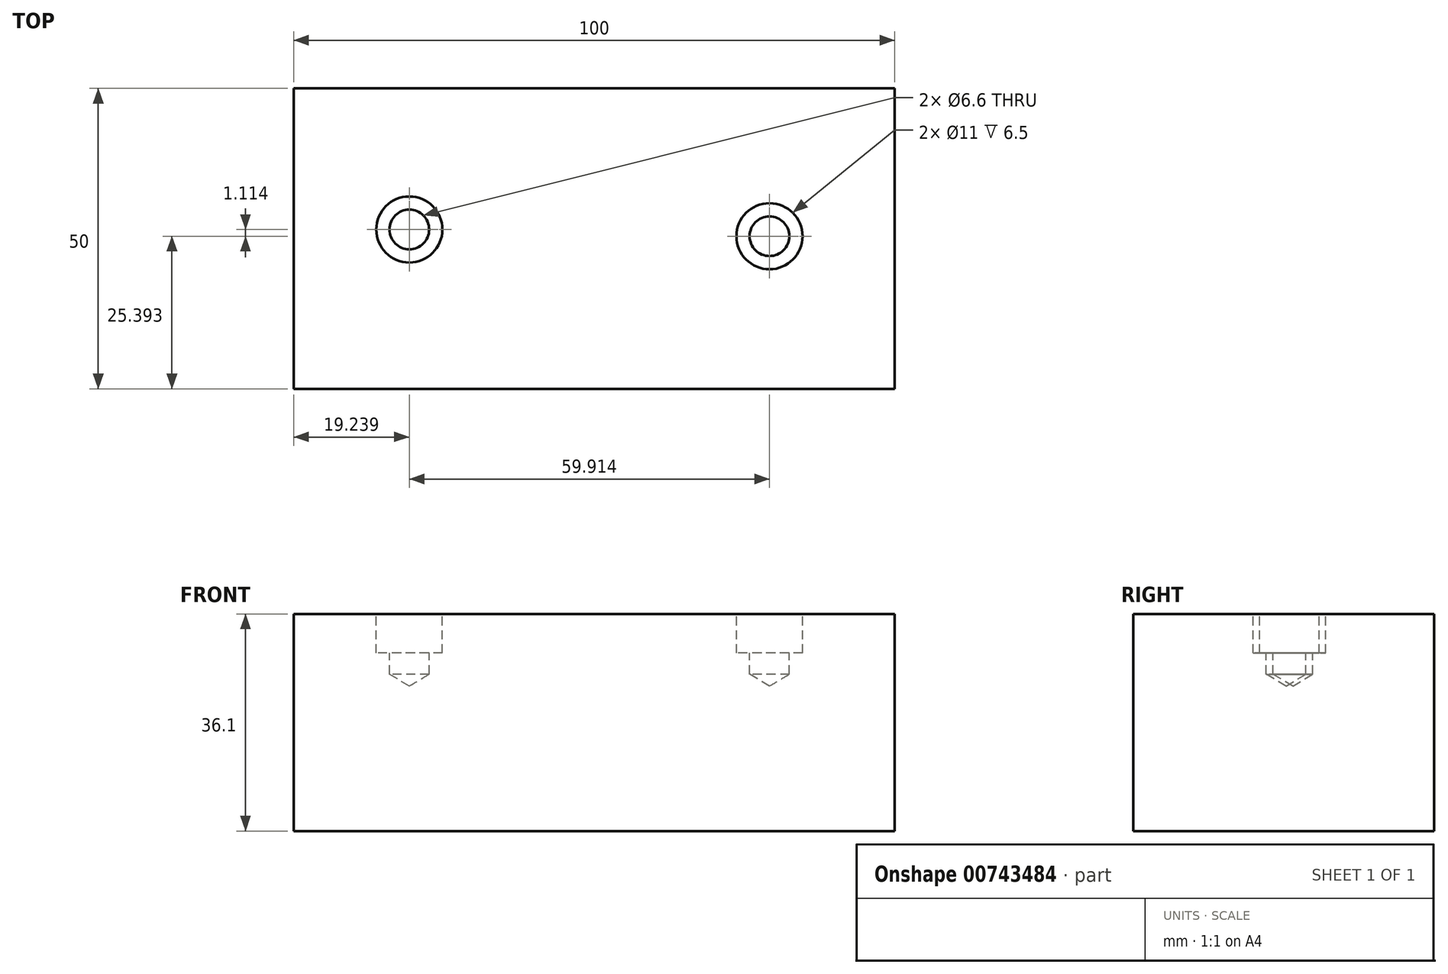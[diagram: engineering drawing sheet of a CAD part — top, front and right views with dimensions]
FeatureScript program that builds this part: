
annotation { "Feature Type Name" : "Feature", "Feature Type Description" : "" }
export const myFeature = defineFeature(function(context is Context, id is Id, definition is map)
    precondition{}
    {
        {
            var Q0;
            Q0=qCreatedBy(makeId("Top.planeOp"),FACE);
            var sketch = newSketch(context, id + "F0", { "sketchPlane" : qUnion([Q0])});
            skLineSegment(sketch, "E0.bottom", {"start": v(-49.11, 16.17) * mm, "end": v(50.89, 16.17) * mm});
            skLineSegment(sketch, "E0.top", {"start": v(-49.11, -33.83) * mm, "end": v(50.89, -33.83) * mm});
            skLineSegment(sketch, "E0.left", {"start": v(-49.11, 16.17) * mm, "end": v(-49.11, -33.83) * mm});
            skLineSegment(sketch, "E0.right", {"start": v(50.89, 16.17) * mm, "end": v(50.89, -33.83) * mm});
            skSolve(sketch);
        }
        {
            var Q0;
            Q0 = qSketchRegion(id + "F0", true);
            extrude(context, id + "F1", {"entities" : qUnion([Q0]), "depth" : 36.1 * mm, "offsetDistance" : 25 * mm});
        }
        {
            var Q0;
            Q0=makeQuery(id+"F1.opExtrude","CAP_FACE",FACE,{"disambiguationData":[OSD([sQuery(id+"F0.wireOp",EDGE,"E0.bottom"),sQuery(id+"F0.wireOp",EDGE,"E0.top"),sQuery(id+"F0.wireOp",EDGE,"E0.left"),sQuery(id+"F0.wireOp",EDGE,"E0.right")])],"isStart":false});
            var sketch = newSketch(context, id + "F2", { "sketchPlane" : qUnion([Q0])});
            skPoint(sketch, "E1", {"position": v(30.04, -8.44) * mm});
            skPoint(sketch, "E2", {"position": v(-29.87, -7.32) * mm});
            skSolve(sketch);
        }
        {
            var Q0;
            Q0=sQuery(id+"F2.wireOp",VERTEX,"E1");
            var Q1;
            Q1=sQuery(id+"F2.wireOp",VERTEX,"E2");
            var Q2;
            Q2=makeQuery(id+"F1.opExtrude","SWEPT_BODY",BODY,{"disambiguationData":[OSD([sQuery(id+"F0.wireOp",EDGE,"E0.bottom"),sQuery(id+"F0.wireOp",EDGE,"E0.top"),sQuery(id+"F0.wireOp",EDGE,"E0.left"),sQuery(id+"F0.wireOp",EDGE,"E0.right")])]});
            hole(context, id + "F3", {"style" : HoleStyle.C_BORE, "endStyle" : HoleEndStyle.BLIND, "holeDiameter" : 6.6 * mm, "cBoreDiameter" : 11 * mm, "cBoreDepth" : 6.5 * mm, "majorDiameter" : 5 * mm, "holeDepth" : 10 * mm, "isTappedThrough" : true, "tappedDepth" : 11.5 * mm, "tapClearance" : 3, "locations" : qUnion([Q0, Q1]), "scope" : qUnion([Q2])});
        }
    });
